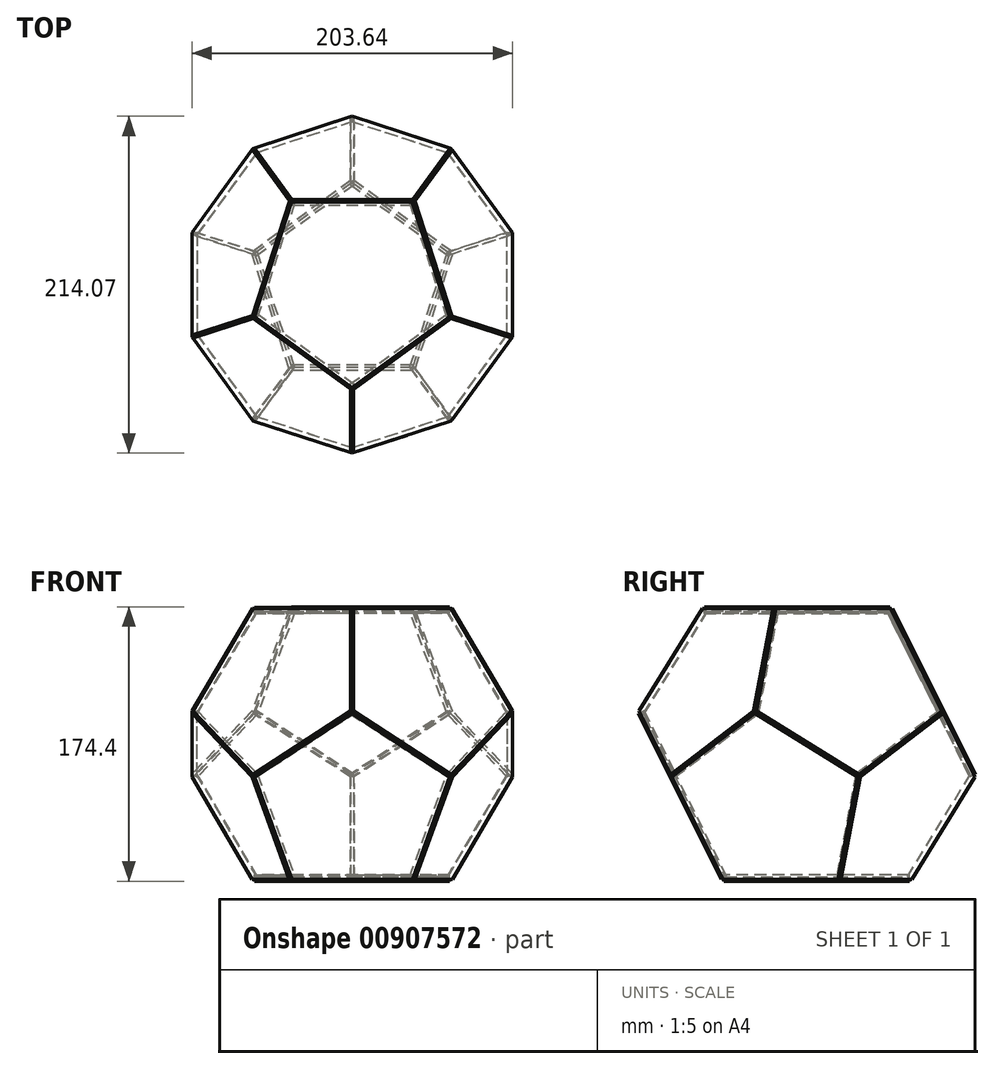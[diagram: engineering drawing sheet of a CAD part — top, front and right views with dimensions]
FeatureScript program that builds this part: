
annotation { "Feature Type Name" : "Feature", "Feature Type Description" : "" }
export const myFeature = defineFeature(function(context is Context, id is Id, definition is map)
    precondition{}
    {
        {
            var Q0;
            Q0=qCreatedBy(makeId("Top.planeOp"),FACE);
            var sketch = newSketch(context, id + "F0", { "sketchPlane" : qUnion([Q0])});
            skCircle(sketch, "E0.cCircle", {"center": v(0, 0) * mm, "radius": 52.66 * mm, "construction": true});
            skLineSegment(sketch, "E0.0", {"start": v(61.9, 20.12) * mm, "end": v(38.26, -52.66) * mm});
            skLineSegment(sketch, "E0.1", {"start": v(38.26, -52.66) * mm, "end": v(-38.26, -52.66) * mm});
            skLineSegment(sketch, "E0.2", {"start": v(-38.26, -52.66) * mm, "end": v(-61.9, 20.12) * mm});
            skLineSegment(sketch, "E0.3", {"start": v(-61.9, 20.12) * mm, "end": v(0, 65.1) * mm});
            skLineSegment(sketch, "E0.4", {"start": v(0, 65.1) * mm, "end": v(61.9, 20.12) * mm});
            skPoint(sketch, "E0.0.midPoint", {"position": v(50.09, -16.27) * mm});
            skSolve(sketch);
        }
        {
            var Q0;
            Q0=makeQuery(id+"F0.imprint","IMPRINT",FACE,{"disambiguationData":[TD([[makeQuery(id+"F0.imprint","IMPRINT",EDGE,{"derivedFrom":sQuery(id+"F0.wireOp",EDGE,"E0.0")}),-1.0]])]});
            extrude(context, id + "F1", {"entities" : qUnion([Q0]), "oppositeDirection" : true, "depth" : 2 * mm, "offsetDistance" : 25.4 * mm, "hasSecondDirection" : true, "secondDirectionOppositeDirection" : false, "secondDirectionDepth" : 2 * mm});
        }
        {
            var Q0;
            Q0=qCreatedBy(makeId("Front.planeOp"),FACE);
            var sketch = newSketch(context, id + "F2", { "sketchPlane" : qUnion([Q0])});
            skLineSegment(sketch, "E1", {"start": v(0, 0) * mm, "end": v(0, 106.17) * mm, "construction": true});
            skSolve(sketch);
        }
        {
            var Q0;
            Q0=makeQuery(id+"F1.opExtrude","SWEPT_BODY",BODY,{"disambiguationData":[OSD([sQuery(id+"F0.wireOp",EDGE,"E0.0"),sQuery(id+"F0.wireOp",EDGE,"E0.1"),sQuery(id+"F0.wireOp",EDGE,"E0.2"),sQuery(id+"F0.wireOp",EDGE,"E0.3"),sQuery(id+"F0.wireOp",EDGE,"E0.4")])]});
            transform(context, id + "F3", {"entities" : qUnion([Q0]), "transformType" : TransformType.COPY});
        }
        {
            var Q0;
            Q0=makeQuery(id+"F3.opPattern","COPY",BODY,{"derivedFrom":makeQuery(id+"F1.opExtrude","SWEPT_BODY",BODY,{"disambiguationData":[OSD([sQuery(id+"F0.wireOp",EDGE,"E0.0"),sQuery(id+"F0.wireOp",EDGE,"E0.1"),sQuery(id+"F0.wireOp",EDGE,"E0.2"),sQuery(id+"F0.wireOp",EDGE,"E0.3"),sQuery(id+"F0.wireOp",EDGE,"E0.4")])]}),"instanceName":"1"});
            var Q1;
            Q1=sQuery(id+"F0.wireOp",EDGE,"E0.4");
            transform(context, id + "F4", {"entities" : qUnion([Q0]), "transformType" : TransformType.ROTATION, "transformAxis" : qUnion([Q1]), "angle" : 116.51 * degree, "oppositeDirection" : true, "makeCopy" : false});
        }
        {
            var Q0;
            Q0=makeQuery(id+"F3.opPattern","COPY",BODY,{"derivedFrom":makeQuery(id+"F1.opExtrude","SWEPT_BODY",BODY,{"disambiguationData":[OSD([sQuery(id+"F0.wireOp",EDGE,"E0.0"),sQuery(id+"F0.wireOp",EDGE,"E0.1"),sQuery(id+"F0.wireOp",EDGE,"E0.2"),sQuery(id+"F0.wireOp",EDGE,"E0.3"),sQuery(id+"F0.wireOp",EDGE,"E0.4")])]}),"instanceName":"1"});
            var Q1;
            Q1=sQuery(id+"F2.wireOp",EDGE,"E1");
            circularPattern(context, id + "F5", {"entities" : qUnion([Q0]), "axis" : qUnion([Q1]), "angle" : 360 * degree, "instanceCount" : 5, "equalSpace" : true});
        }
        {
            var Q0;
            Q0=makeQuery(id+"F3.opPattern","COPY",FACE,{"derivedFrom":makeQuery(id+"F1.opExtrude","SWEPT_FACE",FACE,{"disambiguationData":[OSD([sQuery(id+"F0.wireOp",EDGE,"E0.1")])]}),"instanceName":"1"});
            var sketch = newSketch(context, id + "F6", { "sketchPlane" : qUnion([Q0])});
            skLineSegment(sketch, "E2", {"start": v(-23.08, 92.64) * mm, "end": v(29.66, 37.2) * mm, "construction": true});
            skSolve(sketch);
        }
        {
            var Q0;
            Q0=makeQuery(id+"F3.opPattern","COPY",BODY,{"derivedFrom":makeQuery(id+"F1.opExtrude","SWEPT_BODY",BODY,{"disambiguationData":[OSD([sQuery(id+"F0.wireOp",EDGE,"E0.0"),sQuery(id+"F0.wireOp",EDGE,"E0.1"),sQuery(id+"F0.wireOp",EDGE,"E0.2"),sQuery(id+"F0.wireOp",EDGE,"E0.3"),sQuery(id+"F0.wireOp",EDGE,"E0.4")])]}),"instanceName":"1"});
            transform(context, id + "F7", {"entities" : qUnion([Q0]), "transformType" : TransformType.COPY});
        }
        {
            var Q0;
            Q0=makeQuery(id+"F7.opPattern","COPY",BODY,{"derivedFrom":makeQuery(id+"F3.opPattern","COPY",BODY,{"derivedFrom":makeQuery(id+"F1.opExtrude","SWEPT_BODY",BODY,{"disambiguationData":[OSD([sQuery(id+"F0.wireOp",EDGE,"E0.0"),sQuery(id+"F0.wireOp",EDGE,"E0.1"),sQuery(id+"F0.wireOp",EDGE,"E0.2"),sQuery(id+"F0.wireOp",EDGE,"E0.3"),sQuery(id+"F0.wireOp",EDGE,"E0.4")])]}),"instanceName":"1"}),"instanceName":"1"});
            var Q1;
            Q1=sQuery(id+"F6.wireOp",EDGE,"E2");
            transform(context, id + "F8", {"entities" : qUnion([Q0]), "transformType" : TransformType.ROTATION, "transformAxis" : qUnion([Q1]), "angle" : 116.51 * degree, "oppositeDirection" : true, "makeCopy" : false});
        }
        {
            var Q0;
            Q0=makeQuery(id+"F7.opPattern","COPY",BODY,{"derivedFrom":makeQuery(id+"F3.opPattern","COPY",BODY,{"derivedFrom":makeQuery(id+"F1.opExtrude","SWEPT_BODY",BODY,{"disambiguationData":[OSD([sQuery(id+"F0.wireOp",EDGE,"E0.0"),sQuery(id+"F0.wireOp",EDGE,"E0.1"),sQuery(id+"F0.wireOp",EDGE,"E0.2"),sQuery(id+"F0.wireOp",EDGE,"E0.3"),sQuery(id+"F0.wireOp",EDGE,"E0.4")])]}),"instanceName":"1"}),"instanceName":"1"});
            var Q1;
            Q1=sQuery(id+"F2.wireOp",EDGE,"E1");
            circularPattern(context, id + "F9", {"entities" : qUnion([Q0]), "axis" : qUnion([Q1]), "angle" : 360 * degree, "instanceCount" : 5, "equalSpace" : true});
        }
        {
            var Q0;
            Q0=makeQuery(id+"F7.opPattern","COPY",FACE,{"derivedFrom":makeQuery(id+"F3.opPattern","COPY",FACE,{"derivedFrom":makeQuery(id+"F1.opExtrude","SWEPT_FACE",FACE,{"disambiguationData":[OSD([sQuery(id+"F0.wireOp",EDGE,"E0.3")])]}),"instanceName":"1"}),"instanceName":"1"});
            var sketch = newSketch(context, id + "F10", { "sketchPlane" : qUnion([Q0])});
            skLineSegment(sketch, "E3", {"start": v(102.83, 78.1) * mm, "end": v(128.69, 6.84) * mm, "construction": true});
            skSolve(sketch);
        }
        {
            var Q0;
            Q0=makeQuery(id+"F9.opPattern","COPY",BODY,{"derivedFrom":makeQuery(id+"F7.opPattern","COPY",BODY,{"derivedFrom":makeQuery(id+"F3.opPattern","COPY",BODY,{"derivedFrom":makeQuery(id+"F1.opExtrude","SWEPT_BODY",BODY,{"disambiguationData":[OSD([sQuery(id+"F0.wireOp",EDGE,"E0.0"),sQuery(id+"F0.wireOp",EDGE,"E0.1"),sQuery(id+"F0.wireOp",EDGE,"E0.2"),sQuery(id+"F0.wireOp",EDGE,"E0.3"),sQuery(id+"F0.wireOp",EDGE,"E0.4")])]}),"instanceName":"1"}),"instanceName":"1"}),"instanceName":"4"});
            transform(context, id + "F11", {"entities" : qUnion([Q0]), "transformType" : TransformType.COPY});
        }
        {
            var Q0;
            Q0=makeQuery(id+"F7.opPattern","COPY",BODY,{"derivedFrom":makeQuery(id+"F3.opPattern","COPY",BODY,{"derivedFrom":makeQuery(id+"F1.opExtrude","SWEPT_BODY",BODY,{"disambiguationData":[OSD([sQuery(id+"F0.wireOp",EDGE,"E0.0"),sQuery(id+"F0.wireOp",EDGE,"E0.1"),sQuery(id+"F0.wireOp",EDGE,"E0.2"),sQuery(id+"F0.wireOp",EDGE,"E0.3"),sQuery(id+"F0.wireOp",EDGE,"E0.4")])]}),"instanceName":"1"}),"instanceName":"1"});
            transform(context, id + "F12", {"entities" : qUnion([Q0]), "transformType" : TransformType.COPY});
        }
        {
            var Q0;
            Q0=makeQuery(id+"F11.opPattern","COPY",BODY,{"derivedFrom":makeQuery(id+"F9.opPattern","COPY",BODY,{"derivedFrom":makeQuery(id+"F7.opPattern","COPY",BODY,{"derivedFrom":makeQuery(id+"F3.opPattern","COPY",BODY,{"derivedFrom":makeQuery(id+"F1.opExtrude","SWEPT_BODY",BODY,{"disambiguationData":[OSD([sQuery(id+"F0.wireOp",EDGE,"E0.0"),sQuery(id+"F0.wireOp",EDGE,"E0.1"),sQuery(id+"F0.wireOp",EDGE,"E0.2"),sQuery(id+"F0.wireOp",EDGE,"E0.3"),sQuery(id+"F0.wireOp",EDGE,"E0.4")])]}),"instanceName":"1"}),"instanceName":"1"}),"instanceName":"4"}),"instanceName":"1"});
            deleteBodies(context, id + "F13", {"entities" : qUnion([Q0])});
        }
        {
            var Q0;
            Q0=makeQuery(id+"F12.opPattern","COPY",BODY,{"derivedFrom":makeQuery(id+"F7.opPattern","COPY",BODY,{"derivedFrom":makeQuery(id+"F3.opPattern","COPY",BODY,{"derivedFrom":makeQuery(id+"F1.opExtrude","SWEPT_BODY",BODY,{"disambiguationData":[OSD([sQuery(id+"F0.wireOp",EDGE,"E0.0"),sQuery(id+"F0.wireOp",EDGE,"E0.1"),sQuery(id+"F0.wireOp",EDGE,"E0.2"),sQuery(id+"F0.wireOp",EDGE,"E0.3"),sQuery(id+"F0.wireOp",EDGE,"E0.4")])]}),"instanceName":"1"}),"instanceName":"1"}),"instanceName":"1"});
            var Q1;
            Q1=sQuery(id+"F10.wireOp",EDGE,"E3");
            transform(context, id + "F14", {"entities" : qUnion([Q0]), "transformType" : TransformType.ROTATION, "transformAxis" : qUnion([Q1]), "angle" : 116.51 * degree, "oppositeDirection" : true, "makeCopy" : false});
        }
    });
